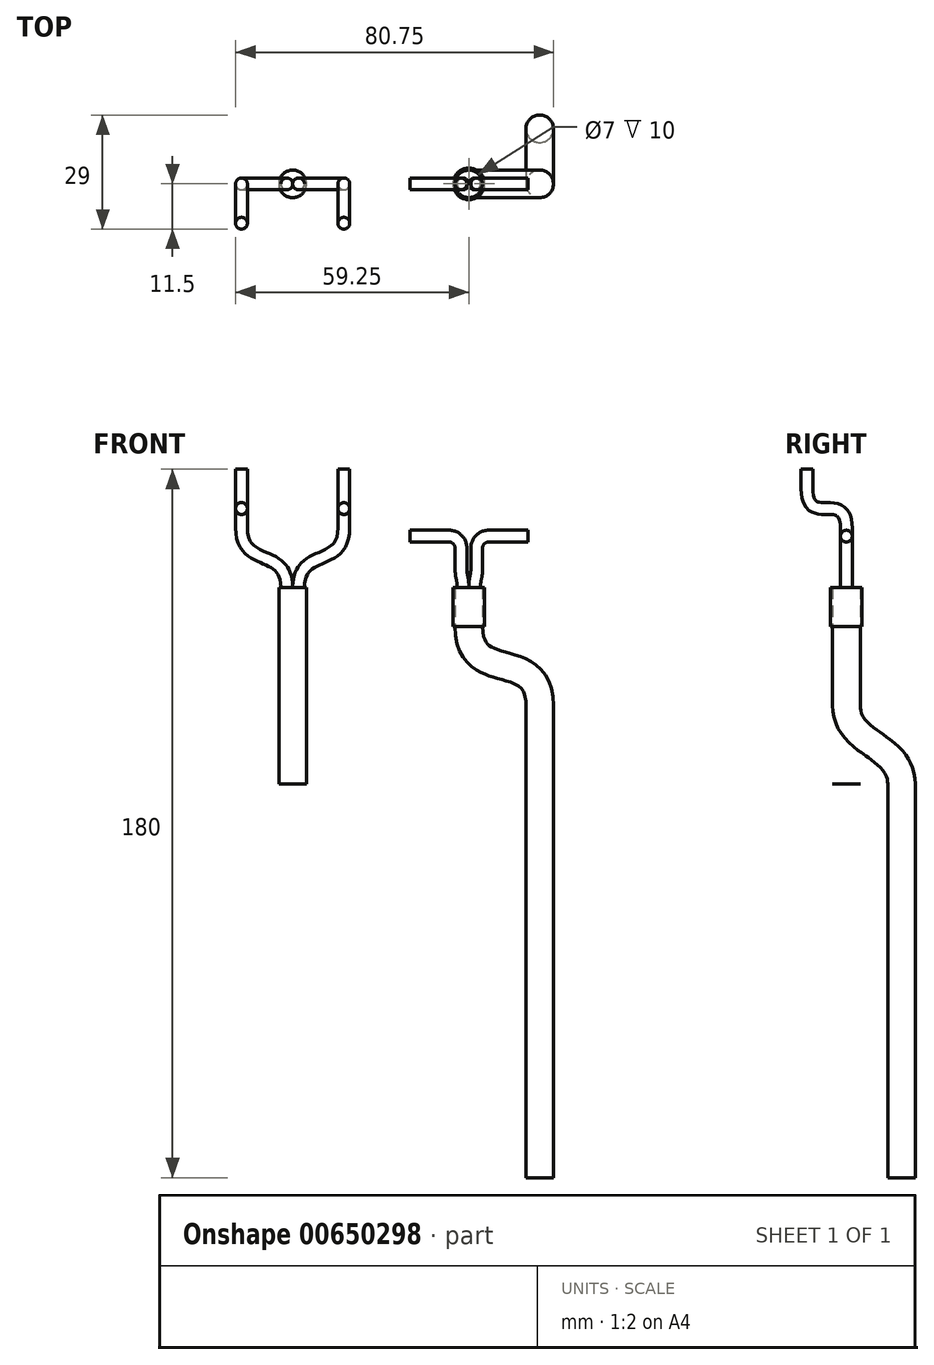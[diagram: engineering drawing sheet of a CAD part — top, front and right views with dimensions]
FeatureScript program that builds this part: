
annotation { "Feature Type Name" : "Feature", "Feature Type Description" : "" }
export const myFeature = defineFeature(function(context is Context, id is Id, definition is map)
    precondition{}
    {
        {
            var Q0;
            Q0=qCreatedBy(makeId("Top.planeOp"),FACE);
            var sketch = newSketch(context, id + "F0", { "sketchPlane" : qUnion([Q0])});
            skCircle(sketch, "E0", {"center": v(0, 0) * mm, "radius": 3.5 * mm});
            skSolve(sketch);
        }
        {
            var Q0;
            Q0=qCreatedBy(makeId("Front.planeOp"),FACE);
            var sketch = newSketch(context, id + "F1", { "sketchPlane" : qUnion([Q0])});
            skLineSegment(sketch, "E1", {"start": v(0, 0) * mm, "end": v(0, -10) * mm});
            skFitSpline(sketch, "E2", {"points": [v(0, -10) * mm, v(18, -30) * mm], "startDerivative": vector(0, -45) * mm, "endDerivative": vector(0, -45) * mm});
            skSolve(sketch);
        }
        {
            var Q0;
            Q0=qCreatedBy(makeId("Right.planeOp"),FACE);
            cPlane(context, id + "F2", {"entities" : qUnion([Q0]), "cplaneType" : CPlaneType.OFFSET, "offset" : 18 * mm, "width" : 150 * mm, "height" : 150 * mm});
        }
        {
            var Q0;
            Q0=qCreatedBy(id+"F2.planeOp",FACE);
            var sketch = newSketch(context, id + "F3", { "sketchPlane" : qUnion([Q0])});
            skFitSpline(sketch, "E3", {"points": [v(0, -30) * mm, v(14, -50) * mm], "startDerivative": vector(0, -30) * mm, "endDerivative": vector(0, -30) * mm});
            skLineSegment(sketch, "E4", {"start": v(14, -50) * mm, "end": v(14, -150) * mm});
            skSolve(sketch);
        }
        {
            var Q0;
            Q0=qSketchRegion(id+"F0",true);
            var Q1;
            Q1=qConstructionFilter(qBodyType(qCreatedBy(id+"F1",EDGE),BodyType.WIRE),ConstructionObject.NO);
            var Q2;
            Q2=qConstructionFilter(qBodyType(qCreatedBy(id+"F3",EDGE),BodyType.WIRE),ConstructionObject.NO);
            sweep(context, id + "F4", {"profiles" : qUnion([Q0]), "path" : qUnion([Q1, Q2])});
        }
        {
            var Q0;
            Q0=makeQuery(id+"F4.opSweep","CAP_FACE",FACE,{"disambiguationData":[OSD([sQuery(id+"F0.wireOp",EDGE,"E0"),sQuery(id+"F1.wireOp",VERTEX,"E1.start")])],"isStart":true});
            var sketch = newSketch(context, id + "F5", { "sketchPlane" : qUnion([Q0])});
            skCircle(sketch, "E5", {"center": v(1.5, 0) * mm, "radius": 1.5 * mm});
            skSolve(sketch);
        }
        {
            var Q0;
            Q0=qCreatedBy(makeId("Front.planeOp"),FACE);
            var sketch = newSketch(context, id + "F6", { "sketchPlane" : qUnion([Q0])});
            skFitSpline(sketch, "E6", {"points": [v(1.5, 0) * mm, v(2, 5) * mm], "startDerivative": vector(0, 9) * mm, "endDerivative": vector(0, 9) * mm});
            skLineSegment(sketch, "E7", {"start": v(2, 5) * mm, "end": v(2, 10) * mm});
            skArc(sketch, "E8", {"start": v(5, 13) * mm, "mid": v(2.88, 12.12) * mm, "end": v(2, 10) * mm});
            skLineSegment(sketch, "E9", {"start": v(5, 13) * mm, "end": v(15, 13) * mm});
            skSolve(sketch);
        }
        {
            var Q0;
            Q0=qSketchRegion(id+"F5",true);
            var Q1;
            Q1=qConstructionFilter(qBodyType(qCreatedBy(id+"F6",EDGE),BodyType.WIRE),ConstructionObject.NO);
            sweep(context, id + "F7", {"profiles" : qUnion([Q0]), "path" : qUnion([Q1])});
        }
        {
            var Q0;
            Q0=makeQuery(id+"F7.opSweep","SWEPT_BODY",BODY,{"disambiguationData":[OSD([sQuery(id+"F5.wireOp",EDGE,"E5"),sQuery(id+"F6.wireOp",EDGE,"E7")])]});
            var Q1;
            Q1=qCreatedBy(makeId("Right.planeOp"),FACE);
            mirror(context, id + "F8", {"entities" : qUnion([Q0]), "mirrorPlane" : qUnion([Q1])});
        }
        {
            var Q0;
            Q0=makeQuery(id+"F4.opSweep","CAP_FACE",FACE,{"disambiguationData":[OSD([sQuery(id+"F0.wireOp",EDGE,"E0"),sQuery(id+"F1.wireOp",VERTEX,"E1.start")])],"isStart":true});
            var sketch = newSketch(context, id + "F9", { "sketchPlane" : qUnion([Q0])});
            skCircle(sketch, "E10.0", {"center": v(0, 0) * mm, "radius": 3.5 * mm});
            skCircle(sketch, "E11.0", {"center": v(0, 0) * mm, "radius": 4 * mm});
            skSolve(sketch);
        }
        {
            var Q0;
            Q0=qSketchRegion(id+"F9",true);
            extrude(context, id + "F10", {"entities" : qUnion([Q0]), "oppositeDirection" : true, "depth" : 10 * mm, "offsetDistance" : 25 * mm});
        }
        {
            var Q0;
            Q0=qCreatedBy(makeId("Top.planeOp"),FACE);
            var sketch = newSketch(context, id + "F11", { "sketchPlane" : qUnion([Q0])});
            skCircle(sketch, "E12", {"center": v(-44.75, 0) * mm, "radius": 3.5 * mm});
            skSolve(sketch);
        }
        {
            var Q0;
            Q0=qSketchRegion(id+"F11",true);
            extrude(context, id + "F12", {"entities" : qUnion([Q0]), "oppositeDirection" : true, "depth" : 50 * mm, "offsetDistance" : 25 * mm});
        }
        {
            var Q0;
            Q0=makeQuery(id+"F12.opExtrude","CAP_FACE",FACE,{"disambiguationData":[OSD([sQuery(id+"F11.wireOp",EDGE,"E12")])],"isStart":true});
            var sketch = newSketch(context, id + "F13", { "sketchPlane" : qUnion([Q0])});
            skCircle(sketch, "E13", {"center": v(-43.25, 0) * mm, "radius": 1.5 * mm});
            skPoint(sketch, "E14", {"position": v(-44.75, 0) * mm});
            skSolve(sketch);
        }
        {
            var Q0;
            Q0=qCreatedBy(makeId("Front.planeOp"),FACE);
            var sketch = newSketch(context, id + "F14", { "sketchPlane" : qUnion([Q0])});
            skFitSpline(sketch, "E15", {"points": [v(-43.25, 0) * mm, v(-37.5, 7.5) * mm, v(-31.75, 15) * mm], "startDerivative": vector(0, 30) * mm, "endDerivative": vector(0, 30) * mm});
            skLineSegment(sketch, "E16", {"start": v(-43.25, 5) * mm, "end": v(-43.25, 0) * mm, "construction": true});
            skLineSegment(sketch, "E17", {"start": v(-31.75, 15) * mm, "end": v(-31.75, 10) * mm, "construction": true});
            skLineSegment(sketch, "E18", {"start": v(-31.75, 15) * mm, "end": v(-43.25, 0) * mm, "construction": true});
            skSolve(sketch);
        }
        {
            var Q0;
            Q0=qCreatedBy(makeId("Right.planeOp"),FACE);
            var Q1;
            Q1=sQuery(id+"F14.wireOp",VERTEX,"E18.start");
            cPlane(context, id + "F15", {"entities" : qUnion([Q0, Q1]), "cplaneType" : CPlaneType.PLANE_POINT, "offset" : 25 * mm, "width" : 150 * mm, "height" : 150 * mm});
        }
        {
            var Q0;
            Q0=qCreatedBy(id+"F15.planeOp",FACE);
            var sketch = newSketch(context, id + "F16", { "sketchPlane" : qUnion([Q0])});
            skFitSpline(sketch, "E19", {"points": [v(0, 15) * mm, v(-5, 20) * mm, v(-10, 25) * mm], "startDerivative": vector(0, 30) * mm, "endDerivative": vector(0, 30) * mm});
            skLineSegment(sketch, "E20", {"start": v(-10, 20) * mm, "end": v(-10, 25) * mm, "construction": true});
            skLineSegment(sketch, "E21", {"start": v(0, 20) * mm, "end": v(0, 15) * mm, "construction": true});
            skLineSegment(sketch, "E22", {"start": v(0, 15) * mm, "end": v(-10, 25) * mm, "construction": true});
            skLineSegment(sketch, "E23", {"start": v(-10, 25) * mm, "end": v(-10, 30) * mm});
            skSolve(sketch);
        }
        {
            var Q0;
            Q0=makeQuery(id+"F13.imprint","IMPRINT",FACE,{"disambiguationData":[TD([[makeQuery(id+"F13.imprint","IMPRINT",EDGE,{"derivedFrom":sQuery(id+"F13.wireOp",EDGE,"E13")}),1.0]])]});
            var Q1;
            Q1=sQuery(id+"F16.wireOp",EDGE,"E19");
            var Q2;
            Q2=sQuery(id+"F14.wireOp",EDGE,"E15");
            var Q3;
            Q3=sQuery(id+"F16.wireOp",EDGE,"E23");
            sweep(context, id + "F17", {"profiles" : qUnion([Q0]), "path" : qUnion([Q1, Q2, Q3])});
        }
        {
            var Q0;
            Q0=qCreatedBy(makeId("Right.planeOp"),FACE);
            var Q1;
            Q1=sQuery(id+"F13.wireOp",VERTEX,"E14");
            cPlane(context, id + "F18", {"entities" : qUnion([Q0, Q1]), "cplaneType" : CPlaneType.PLANE_POINT, "offset" : 25 * mm, "width" : 150 * mm, "height" : 150 * mm});
        }
        {
            var Q0;
            Q0=makeQuery(id+"F17.opSweep","SWEPT_BODY",BODY,{"disambiguationData":[OSD([sQuery(id+"F13.wireOp",EDGE,"E13"),sQuery(id+"F14.wireOp",EDGE,"E15")])]});
            var Q1;
            Q1=qCreatedBy(id+"F18.planeOp",FACE);
            mirror(context, id + "F19", {"entities" : qUnion([Q0]), "mirrorPlane" : qUnion([Q1])});
        }
    });
